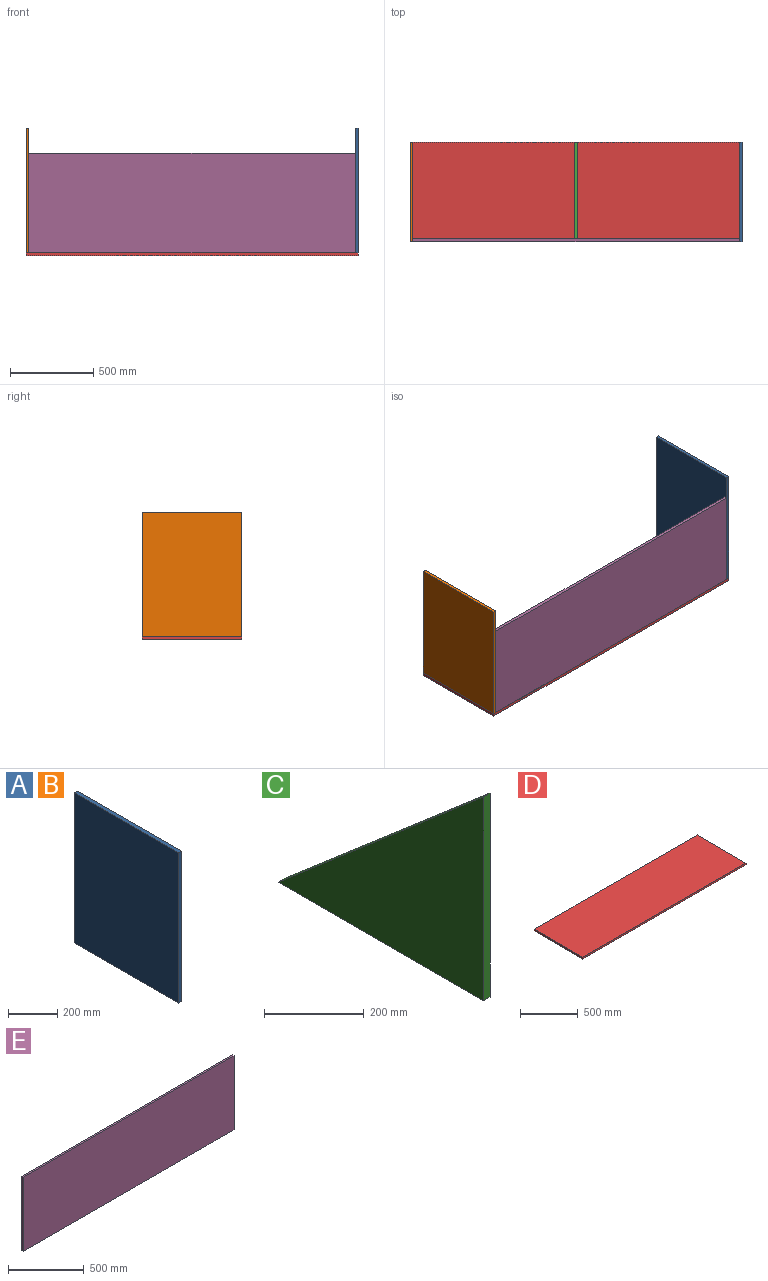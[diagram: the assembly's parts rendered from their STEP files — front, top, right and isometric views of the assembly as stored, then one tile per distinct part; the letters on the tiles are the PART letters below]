
ASSEMBLY  parts=5 mates=4
PART A: 6 faces, bbox 18x600x750 mm
  f0: plane 750x18mm, normal (0,1,0), area 13500mm2, adj f1,f3,f4,f5
  f1: plane 750x600mm, normal (-1,0,0), area 450000mm2, adj f0,f2,f4,f5
  f2: plane 750x18mm, normal (0,-1,0), area 13500mm2, adj f1,f3,f4,f5
  f3: plane 750x600mm, normal (1,0,0), area 450000mm2, adj f0,f2,f4,f5
  f4: plane 600x18mm, normal (0,0,1), area 10800mm2, adj f0,f1,f2,f3
  f5: plane 600x18mm, normal (0,0,-1), area 10800mm2, adj f0,f1,f2,f3
PART B: same geometry as A
PART C: 5 faces, bbox 18x582x500 mm
  f0: plane 500x18mm, normal (0,-1,0), area 9000mm2, adj f1,f2,f3,f4
  f1: plane 582x500mm, normal (0,0.65,0.76), area 13811.1mm2, adj f0,f2,f3,f4
  f2: plane 582x18mm, normal (0,0,-1), area 10476mm2, adj f0,f1,f3,f4
  f3: plane 582x500mm, normal (-1,0,0), area 145500mm2, adj f0,f1,f2
  f4: plane 582x500mm, normal (1,0,0), area 145500mm2, adj f0,f1,f2
PART D: 6 faces, bbox 2000x600x18 mm
  f0: plane 2000x18mm, normal (0,1,0), area 36000mm2, adj f1,f3,f4,f5
  f1: plane 600x18mm, normal (-1,0,0), area 10800mm2, adj f0,f2,f4,f5
  f2: plane 2000x18mm, normal (0,-1,0), area 36000mm2, adj f1,f3,f4,f5
  f3: plane 600x18mm, normal (1,0,0), area 10800mm2, adj f0,f2,f4,f5
  f4: plane 2000x600mm, normal (0,0,1), area 1200000mm2, adj f0,f1,f2,f3
  f5: plane 2000x600mm, normal (0,0,-1), area 1200000mm2, adj f0,f1,f2,f3
PART E: 6 faces, bbox 1964x18x600 mm
  f0: plane 1964x600mm, normal (0,1,0), area 1178400mm2, adj f1,f3,f4,f5
  f1: plane 600x18mm, normal (-1,0,0), area 10800mm2, adj f0,f2,f4,f5
  f2: plane 1964x600mm, normal (0,-1,0), area 1178400mm2, adj f1,f3,f4,f5
  f3: plane 600x18mm, normal (1,0,0), area 10800mm2, adj f0,f2,f4,f5
  f4: plane 1964x18mm, normal (0,0,1), area 35352mm2, adj f0,f1,f2,f3
  f5: plane 1964x18mm, normal (0,0,-1), area 35352mm2, adj f0,f1,f2,f3
PLACE A t=(-1426.37,438.3,573.74)mm
PLACE B t=(-3408.37,438.3,573.74)mm
PLACE C t=(-2399.37,438.3,573.74)mm
PLACE D t=(-1426.37,438.3,573.74)mm fixed
PLACE E t=(-1426.37,438.3,573.74)mm
MATE fastened D.f4 <-> A.f5  axis (0,0,1) through (-424.06,-347.05,591.74)mm
MATE fastened E.f0 <-> C.f0  axis (0,1,0) through (-1424.06,-329.05,591.74)mm
MATE fastened A.f1 <-> E.f3  axis (-1,0,0) through (-442.06,-347.05,591.74)mm
MATE fastened D.f4 <-> B.f5  axis (0,0,1) through (-2424.06,-347.05,591.74)mm
